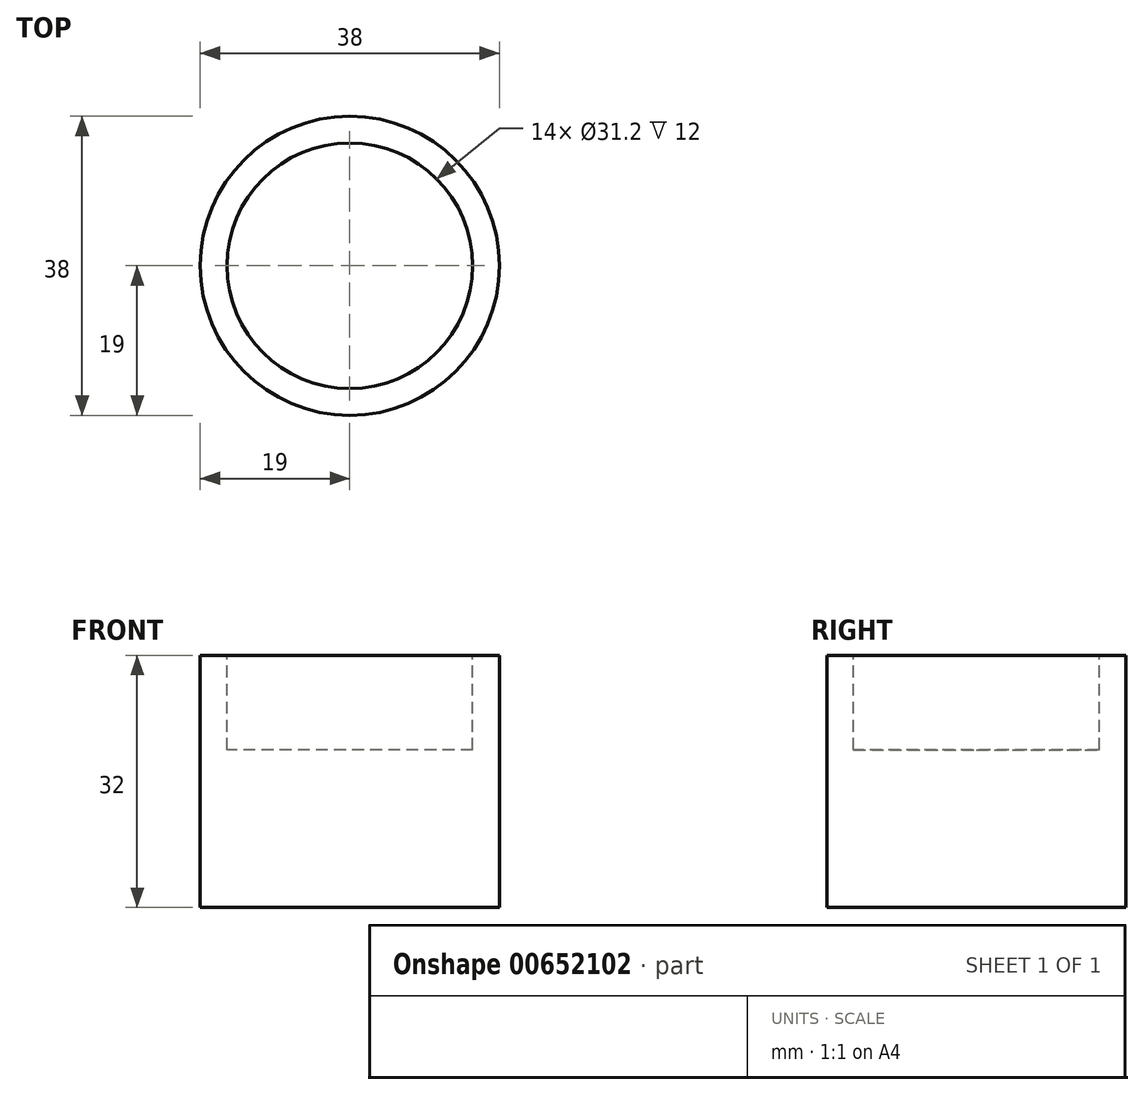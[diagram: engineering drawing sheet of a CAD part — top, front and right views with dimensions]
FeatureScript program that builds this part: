
annotation { "Feature Type Name" : "Feature", "Feature Type Description" : "" }
export const myFeature = defineFeature(function(context is Context, id is Id, definition is map)
    precondition{}
    {
        {
            var Q0;
            Q0=qCreatedBy(makeId("Top.planeOp"),FACE);
            var sketch = newSketch(context, id + "F0", { "sketchPlane" : qUnion([Q0])});
            skCircle(sketch, "E0", {"center": v(0, 0) * mm, "radius": 19 * mm});
            skSolve(sketch);
        }
        {
            var Q0;
            Q0=qSketchRegion(id+"F0",true);
            extrude(context, id + "F1", {"entities" : qUnion([Q0]), "depth" : 32 * mm, "offsetDistance" : 25 * mm});
        }
        {
            var Q0;
            Q0=makeQuery(id+"F1.opExtrude","CAP_FACE",FACE,{"disambiguationData":[OSD([sQuery(id+"F0.wireOp",EDGE,"E0")])],"isStart":false});
            var sketch = newSketch(context, id + "F2", { "sketchPlane" : qUnion([Q0])});
            skCircle(sketch, "E1", {"center": v(0, 0) * mm, "radius": 15.6 * mm});
            skSolve(sketch);
        }
        {
            var Q0;
            Q0=qSketchRegion(id+"F2",true);
            extrude(context, id + "F3", {"entities" : qUnion([Q0]), "operationType" : NewBodyOperationType.REMOVE, "oppositeDirection" : true, "depth" : 12 * mm, "offsetDistance" : 25 * mm});
        }
    });
